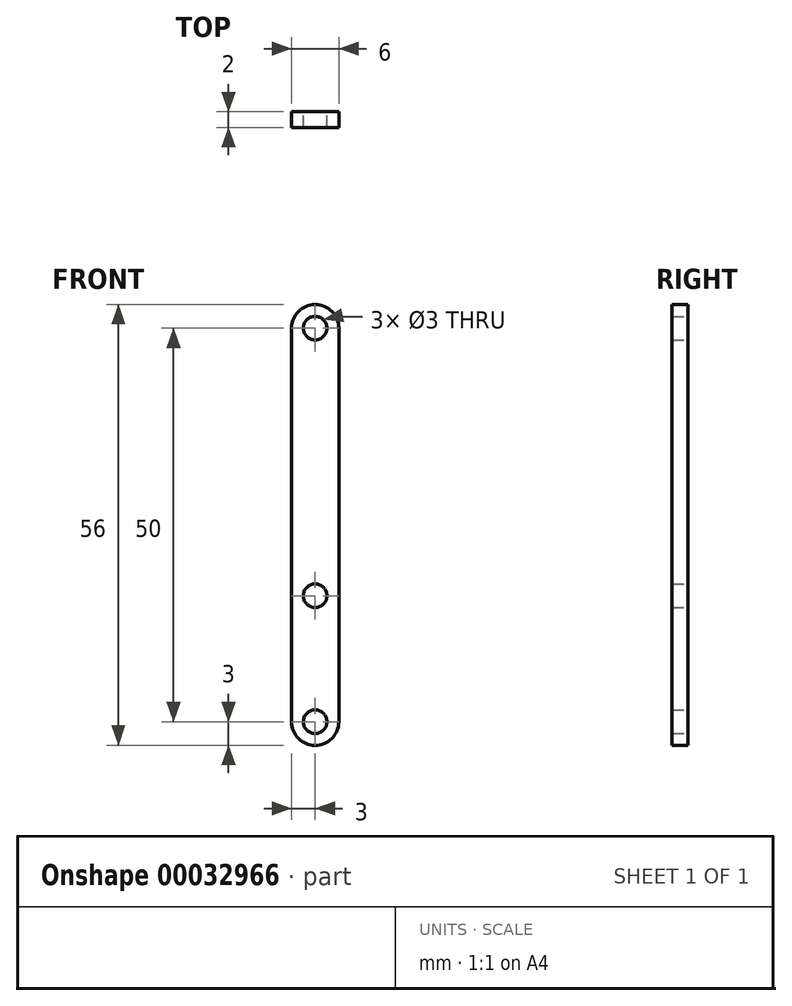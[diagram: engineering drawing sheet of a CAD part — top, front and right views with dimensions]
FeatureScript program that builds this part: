
annotation { "Feature Type Name" : "Feature", "Feature Type Description" : "" }
export const myFeature = defineFeature(function(context is Context, id is Id, definition is map)
    precondition{}
    {
        {
            var Q0;
            Q0=qCreatedBy(makeId("Front.planeOp"),FACE);
            var sketch = newSketch(context, id + "F0", { "sketchPlane" : qUnion([Q0])});
            skLineSegment(sketch, "E0.rect.left", {"start": v(3, -25) * mm, "end": v(3, 25) * mm});
            skLineSegment(sketch, "E0.rect.right", {"start": v(-3, -25) * mm, "end": v(-3, 25) * mm});
            skPoint(sketch, "E0.rect.middle", {"position": v(0, 0) * mm});
            skArc(sketch, "E1", {"start": v(3, 25) * mm, "mid": v(0, 28) * mm, "end": v(-3, 25) * mm});
            skArc(sketch, "E2.MirrorCS", {"start": v(3, -25) * mm, "mid": v(0, -28) * mm, "end": v(-3, -25) * mm});
            skCircle(sketch, "E3", {"center": v(0, 25) * mm, "radius": 1.5 * mm});
            skCircle(sketch, "E4.MirrorC", {"center": v(0, -25) * mm, "radius": 1.5 * mm});
            skCircle(sketch, "E5", {"center": v(0, -9) * mm, "radius": 1.5 * mm});
            skSolve(sketch);
        }
        {
            var Q0;
            Q0=qSketchRegion(id+"F0",true);
            extrude(context, id + "F1", {"entities" : qUnion([Q0]), "depth" : 2 * mm});
        }
    });
